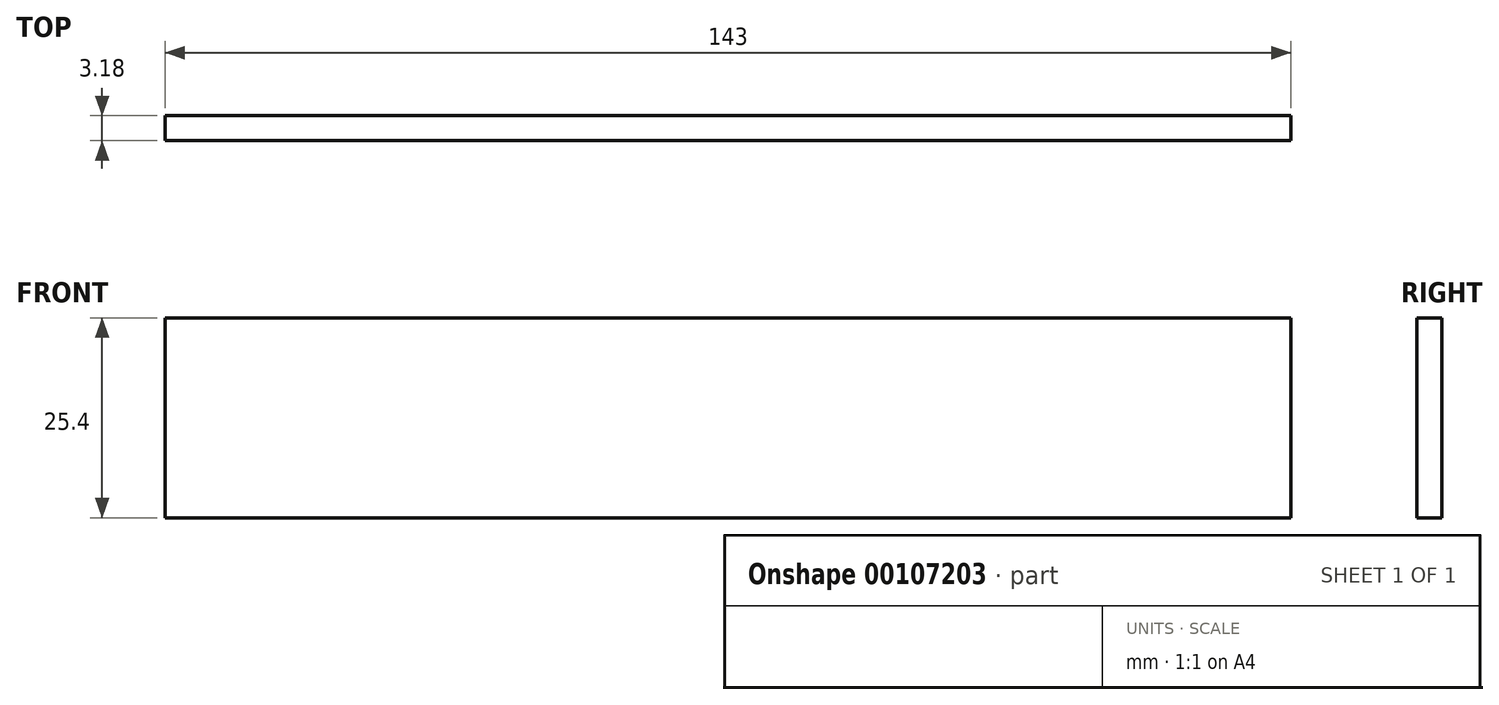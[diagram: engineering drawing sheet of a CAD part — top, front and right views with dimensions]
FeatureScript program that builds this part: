
annotation { "Feature Type Name" : "Feature", "Feature Type Description" : "" }
export const myFeature = defineFeature(function(context is Context, id is Id, definition is map)
    precondition{}
    {
        {
            var Q0;
            Q0=qCreatedBy(makeId("Top.planeOp"),FACE);
            var sketch = newSketch(context, id + "F0", { "sketchPlane" : qUnion([Q0])});
            skLineSegment(sketch, "E0.bottom", {"start": v(-71.5, 1.59) * mm, "end": v(71.5, 1.59) * mm});
            skLineSegment(sketch, "E0.top", {"start": v(-71.5, -1.59) * mm, "end": v(71.5, -1.59) * mm});
            skLineSegment(sketch, "E0.left", {"start": v(-71.5, 1.59) * mm, "end": v(-71.5, -1.59) * mm});
            skLineSegment(sketch, "E0.right", {"start": v(71.5, 1.59) * mm, "end": v(71.5, -1.59) * mm});
            skPoint(sketch, "E0.middle", {"position": v(0, 0) * mm});
            skSolve(sketch);
        }
        {
            var Q0;
            Q0=makeQuery(id+"F0.imprint","IMPRINT",FACE,{"disambiguationData":[TD([[makeQuery(id+"F0.imprint","IMPRINT",EDGE,{"derivedFrom":sQuery(id+"F0.wireOp",EDGE,"E0.bottom")}),-1.0]])]});
            extrude(context, id + "F1", {"entities" : qUnion([Q0]), "depth" : 25.4 * mm});
        }
    });
